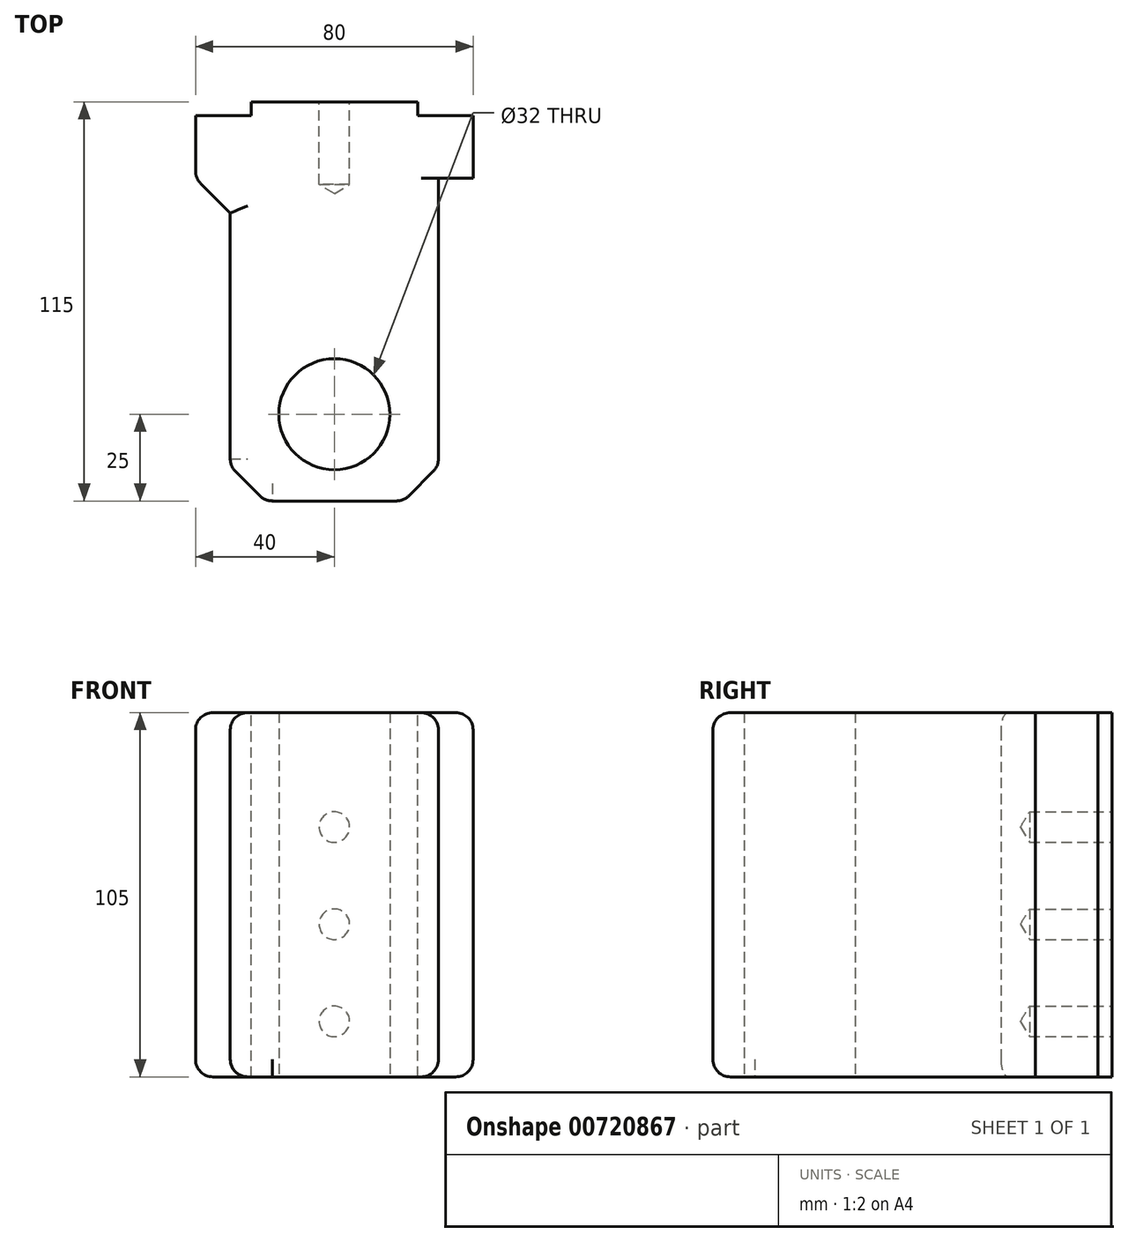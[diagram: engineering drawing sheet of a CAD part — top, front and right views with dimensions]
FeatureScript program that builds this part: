
annotation { "Feature Type Name" : "Feature", "Feature Type Description" : "" }
export const myFeature = defineFeature(function(context is Context, id is Id, definition is map)
    precondition{}
    {
        {
            var Q0;
            Q0=qCreatedBy(makeId("Front.planeOp"),FACE);
            var sketch = newSketch(context, id + "F0", { "sketchPlane" : qUnion([Q0])});
            skLineSegment(sketch, "E0.bottom", {"start": v(0, 0) * mm, "end": v(80, 0) * mm});
            skLineSegment(sketch, "E0.top", {"start": v(0, 105) * mm, "end": v(80, 105) * mm});
            skLineSegment(sketch, "E0.left", {"start": v(0, 0) * mm, "end": v(0, 105) * mm});
            skLineSegment(sketch, "E0.right", {"start": v(80, 0) * mm, "end": v(80, 105) * mm});
            skSolve(sketch);
        }
        {
            var Q0;
            Q0=makeQuery(id+"F0.imprint","IMPRINT",FACE,{"disambiguationData":[TD([[makeQuery(id+"F0.imprint","IMPRINT",EDGE,{"derivedFrom":sQuery(id+"F0.wireOp",EDGE,"E0.bottom")}),1.0]])]});
            extrude(context, id + "F1", {"entities" : qUnion([Q0]), "depth" : 22 * mm, "offsetDistance" : 25 * mm});
        }
        {
            var Q0;
            Q0=makeQuery(id+"F1.opExtrude","CAP_FACE",FACE,{"disambiguationData":[OSD([sQuery(id+"F0.wireOp",EDGE,"E0.bottom"),sQuery(id+"F0.wireOp",EDGE,"E0.top"),sQuery(id+"F0.wireOp",EDGE,"E0.left"),sQuery(id+"F0.wireOp",EDGE,"E0.right")])],"isStart":false});
            var sketch = newSketch(context, id + "F2", { "sketchPlane" : qUnion([Q0])});
            skPoint(sketch, "E1", {"position": v(10, 0) * mm});
            skLineSegment(sketch, "E2.bottom", {"start": v(10, 0) * mm, "end": v(70, 0) * mm});
            skLineSegment(sketch, "E2.top", {"start": v(10, 105) * mm, "end": v(70, 105) * mm});
            skLineSegment(sketch, "E2.left", {"start": v(10, 0) * mm, "end": v(10, 105) * mm});
            skLineSegment(sketch, "E2.right", {"start": v(70, 0) * mm, "end": v(70, 105) * mm});
            skSolve(sketch);
        }
        {
            var Q0;
            Q0=makeQuery(id+"F2.imprint","IMPRINT",FACE,{"disambiguationData":[TD([[makeQuery(id+"F2.imprint","IMPRINT",EDGE,{"derivedFrom":sQuery(id+"F2.wireOp",EDGE,"E2.bottom")}),1.0]])]});
            extrude(context, id + "F3", {"entities" : qUnion([Q0]), "operationType" : NewBodyOperationType.ADD, "depth" : 93 * mm, "offsetDistance" : 25 * mm});
        }
        {
            var Q0;
            Q0=makeQuery(id+"F3.opExtrude","CAP_EDGE",EDGE,{"disambiguationData":[OSD([sQuery(id+"F2.wireOp",EDGE,"E2.left")])],"isStart":true});
            var Q1;
            Q1=makeQuery(id+"F3.opExtrude","CAP_EDGE",EDGE,{"disambiguationData":[OSD([sQuery(id+"F2.wireOp",EDGE,"E2.right")])],"isStart":true});
            var Q2;
            Q2=makeQuery(id+"F3.opExtrude","CAP_EDGE",EDGE,{"disambiguationData":[OSD([sQuery(id+"F2.wireOp",EDGE,"E2.right")])],"isStart":false});
            var Q3;
            Q3=makeQuery(id+"F3.opExtrude","CAP_EDGE",EDGE,{"disambiguationData":[OSD([sQuery(id+"F2.wireOp",EDGE,"E2.left")])],"isStart":false});
            chamfer(context, id + "F4", {"entities" : qUnion([Q0, Q1, Q2, Q3]), "width" : 10 * mm, "tangentPropagation" : true});
        }
        {
            var Q0;
            Q0=makeQuery(id+"F1.opExtrude","CAP_FACE",FACE,{"disambiguationData":[OSD([sQuery(id+"F0.wireOp",EDGE,"E0.bottom"),sQuery(id+"F0.wireOp",EDGE,"E0.top"),sQuery(id+"F0.wireOp",EDGE,"E0.left"),sQuery(id+"F0.wireOp",EDGE,"E0.right")])],"isStart":true});
            var sketch = newSketch(context, id + "F5", { "sketchPlane" : qUnion([Q0])});
            skPoint(sketch, "E3", {"position": v(-64, 0) * mm});
            skPoint(sketch, "E4", {"position": v(-16, 0) * mm});
            skPoint(sketch, "E5", {"position": v(-40, 16) * mm});
            skPoint(sketch, "E5.positionSnap0", {"position": v(-40, 0) * mm});
            skPoint(sketch, "E6", {"position": v(-40, 44) * mm});
            skPoint(sketch, "E7", {"position": v(-40, 72) * mm});
            skLineSegment(sketch, "E8.bottom", {"start": v(-64, 0) * mm, "end": v(-80, 0) * mm});
            skLineSegment(sketch, "E8.top", {"start": v(-64, 105) * mm, "end": v(-80, 105) * mm});
            skLineSegment(sketch, "E8.left", {"start": v(-64, 0) * mm, "end": v(-64, 105) * mm});
            skLineSegment(sketch, "E8.right", {"start": v(-80, 0) * mm, "end": v(-80, 105) * mm});
            skLineSegment(sketch, "E9.bottom", {"start": v(-16, 0) * mm, "end": v(0, 0) * mm});
            skLineSegment(sketch, "E9.top", {"start": v(-16, 105) * mm, "end": v(0, 105) * mm});
            skLineSegment(sketch, "E9.left", {"start": v(-16, 0) * mm, "end": v(-16, 105) * mm});
            skLineSegment(sketch, "E9.right", {"start": v(0, 0) * mm, "end": v(0, 105) * mm});
            skSolve(sketch);
        }
        {
            var Q0;
            Q0=makeQuery(id+"F5.imprint","IMPRINT",FACE,{"disambiguationData":[TD([[makeQuery(id+"F5.imprint","IMPRINT",EDGE,{"derivedFrom":sQuery(id+"F5.wireOp",EDGE,"E8.bottom")}),-1.0]])]});
            var Q1;
            Q1=makeQuery(id+"F5.imprint","IMPRINT",FACE,{"disambiguationData":[TD([[makeQuery(id+"F5.imprint","IMPRINT",EDGE,{"derivedFrom":sQuery(id+"F5.wireOp",EDGE,"E9.bottom")}),-1.0]])]});
            extrude(context, id + "F6", {"entities" : qUnion([Q0, Q1]), "operationType" : NewBodyOperationType.REMOVE, "oppositeDirection" : true, "depth" : 3.96 * mm, "offsetDistance" : 25 * mm});
        }
        {
            var Q0;
            Q0=sQuery(id+"F5.wireOp",VERTEX,"E7");
            var Q1;
            Q1=sQuery(id+"F5.wireOp",VERTEX,"E6");
            var Q2;
            Q2=sQuery(id+"F5.wireOp",VERTEX,"E5");
            var Q3;
            Q3=makeQuery(id+"F1.opExtrude","SWEPT_BODY",BODY,{"disambiguationData":[OSD([sQuery(id+"F0.wireOp",EDGE,"E0.bottom"),sQuery(id+"F0.wireOp",EDGE,"E0.top"),sQuery(id+"F0.wireOp",EDGE,"E0.left"),sQuery(id+"F0.wireOp",EDGE,"E0.right")])]});
            hole(context, id + "F7", {"style" : HoleStyle.SIMPLE, "endStyle" : HoleEndStyle.BLIND, "standardTappedOrClearance" : lookupTablePath({ "standard" : "ISO", "engagement" : "75%", "pitch" : "1.25 mm", "size" : "M10", "type" : "Tapped" }), "standardBlindInLast" : lookupTablePath({ "standard" : "ISO", "engagement" : "75%", "pitch" : "1.25 mm", "size" : "M10", "type" : "Tapped" }), "holeDiameter" : 8.8 * mm, "majorDiameter" : 10 * mm, "showTappedDepth" : true, "holeDepth" : 23.75 * mm, "isTappedThrough" : true, "tappedDepth" : 20 * mm, "tapClearance" : 3, "locations" : qUnion([Q0, Q1, Q2]), "scope" : qUnion([Q3])});
        }
        {
            var Q0;
            Q0=makeQuery(id+"F3.boolean.opBoolean","MERGE",FACE,{"derivedFrom":[makeQuery(id+"F1.opExtrude","SWEPT_FACE",FACE,{"disambiguationData":[OSD([sQuery(id+"F0.wireOp",EDGE,"E0.bottom")])]}),makeQuery(id+"F3.opExtrude","SWEPT_FACE",FACE,{"disambiguationData":[OSD([sQuery(id+"F2.wireOp",EDGE,"E2.bottom")])]})]});
            var sketch = newSketch(context, id + "F8", { "sketchPlane" : qUnion([Q0])});
            skPoint(sketch, "E10", {"position": v(40, 90) * mm});
            skPoint(sketch, "E10.positionSnap0", {"position": v(40, 115) * mm});
            skCircle(sketch, "E11", {"center": v(40, 90) * mm, "radius": 16 * mm});
            skSolve(sketch);
        }
        {
            var Q0;
            Q0=makeQuery(id+"F8.imprint","IMPRINT",FACE,{"disambiguationData":[TD([[makeQuery(id+"F8.imprint","IMPRINT",EDGE,{"derivedFrom":sQuery(id+"F8.wireOp",EDGE,"E11")}),1.0]])]});
            extrude(context, id + "F9", {"entities" : qUnion([Q0]), "operationType" : NewBodyOperationType.REMOVE, "oppositeDirection" : true, "depth" : 120 * mm, "offsetDistance" : 25 * mm});
        }
        {
            var Q0;
            Q0=makeQuery(id+"F3.opExtrude","SWEPT_EDGE",EDGE,{"disambiguationData":[OSD([sQuery(id+"F0.wireOp",EDGE,"E0.top"),sQuery(id+"F2.wireOp",EDGE,"E2.top"),sQuery(id+"F2.wireOp",EDGE,"E2.right")])]});
            var Q1;
            Q1=makeQuery(id+"F4.opChamfer","BLEND_EDGE",EDGE,{"blendedFrom":[makeQuery(id+"F3.opExtrude","CAP_EDGE",EDGE,{"disambiguationData":[OSD([sQuery(id+"F2.wireOp",EDGE,"E2.right")])],"isStart":false}),makeQuery(id+"F3.boolean.opBoolean","MERGE",FACE,{"derivedFrom":[makeQuery(id+"F1.opExtrude","SWEPT_FACE",FACE,{"disambiguationData":[OSD([sQuery(id+"F0.wireOp",EDGE,"E0.top")])]}),makeQuery(id+"F3.opExtrude","SWEPT_FACE",FACE,{"disambiguationData":[OSD([sQuery(id+"F2.wireOp",EDGE,"E2.top")])]})]})],"blendedInto":[makeQuery(id+"F3.boolean.opBoolean","MERGE",FACE,{"derivedFrom":[makeQuery(id+"F1.opExtrude","SWEPT_FACE",FACE,{"disambiguationData":[OSD([sQuery(id+"F0.wireOp",EDGE,"E0.top")])]}),makeQuery(id+"F3.opExtrude","SWEPT_FACE",FACE,{"disambiguationData":[OSD([sQuery(id+"F2.wireOp",EDGE,"E2.top")])]})]})]});
            var Q2;
            Q2=makeQuery(id+"F3.opExtrude","CAP_EDGE",EDGE,{"disambiguationData":[OSD([sQuery(id+"F2.wireOp",EDGE,"E2.top")])],"isStart":false});
            var Q3;
            Q3=makeQuery(id+"F4.opChamfer","BLEND_EDGE",EDGE,{"blendedFrom":[makeQuery(id+"F3.opExtrude","CAP_EDGE",EDGE,{"disambiguationData":[OSD([sQuery(id+"F2.wireOp",EDGE,"E2.left")])],"isStart":false}),makeQuery(id+"F3.boolean.opBoolean","MERGE",FACE,{"derivedFrom":[makeQuery(id+"F1.opExtrude","SWEPT_FACE",FACE,{"disambiguationData":[OSD([sQuery(id+"F0.wireOp",EDGE,"E0.top")])]}),makeQuery(id+"F3.opExtrude","SWEPT_FACE",FACE,{"disambiguationData":[OSD([sQuery(id+"F2.wireOp",EDGE,"E2.top")])]})]})],"blendedInto":[makeQuery(id+"F3.boolean.opBoolean","MERGE",FACE,{"derivedFrom":[makeQuery(id+"F1.opExtrude","SWEPT_FACE",FACE,{"disambiguationData":[OSD([sQuery(id+"F0.wireOp",EDGE,"E0.top")])]}),makeQuery(id+"F3.opExtrude","SWEPT_FACE",FACE,{"disambiguationData":[OSD([sQuery(id+"F2.wireOp",EDGE,"E2.top")])]})]})]});
            var Q4;
            Q4=makeQuery(id+"F3.opExtrude","SWEPT_EDGE",EDGE,{"disambiguationData":[OSD([sQuery(id+"F0.wireOp",EDGE,"E0.top"),sQuery(id+"F2.wireOp",EDGE,"E2.top"),sQuery(id+"F2.wireOp",EDGE,"E2.left")])]});
            var Q5;
            Q5=makeQuery(id+"F4.opChamfer","BLEND_EDGE",EDGE,{"blendedFrom":[makeQuery(id+"F3.opExtrude","CAP_EDGE",EDGE,{"disambiguationData":[OSD([sQuery(id+"F2.wireOp",EDGE,"E2.left")])],"isStart":true}),makeQuery(id+"F3.boolean.opBoolean","MERGE",FACE,{"derivedFrom":[makeQuery(id+"F1.opExtrude","SWEPT_FACE",FACE,{"disambiguationData":[OSD([sQuery(id+"F0.wireOp",EDGE,"E0.top")])]}),makeQuery(id+"F3.opExtrude","SWEPT_FACE",FACE,{"disambiguationData":[OSD([sQuery(id+"F2.wireOp",EDGE,"E2.top")])]})]})],"blendedInto":[makeQuery(id+"F3.boolean.opBoolean","MERGE",FACE,{"derivedFrom":[makeQuery(id+"F1.opExtrude","SWEPT_FACE",FACE,{"disambiguationData":[OSD([sQuery(id+"F0.wireOp",EDGE,"E0.top")])]}),makeQuery(id+"F3.opExtrude","SWEPT_FACE",FACE,{"disambiguationData":[OSD([sQuery(id+"F2.wireOp",EDGE,"E2.top")])]})]})]});
            var Q6;
            Q6=makeQuery(id+"F1.opExtrude","SWEPT_EDGE",EDGE,{"disambiguationData":[OSD([sQuery(id+"F0.wireOp",EDGE,"E0.top"),sQuery(id+"F0.wireOp",EDGE,"E0.left")])]});
            var Q7;
            Q7=makeQuery(id+"F1.opExtrude","SWEPT_EDGE",EDGE,{"disambiguationData":[OSD([sQuery(id+"F0.wireOp",EDGE,"E0.top"),sQuery(id+"F0.wireOp",EDGE,"E0.right")])]});
            var Q8;
            Q8=makeQuery(id+"F4.opChamfer","BLEND_EDGE",EDGE,{"blendedFrom":[makeQuery(id+"F3.opExtrude","CAP_EDGE",EDGE,{"disambiguationData":[OSD([sQuery(id+"F2.wireOp",EDGE,"E2.right")])],"isStart":true}),makeQuery(id+"F3.boolean.opBoolean","MERGE",FACE,{"derivedFrom":[makeQuery(id+"F1.opExtrude","SWEPT_FACE",FACE,{"disambiguationData":[OSD([sQuery(id+"F0.wireOp",EDGE,"E0.top")])]}),makeQuery(id+"F3.opExtrude","SWEPT_FACE",FACE,{"disambiguationData":[OSD([sQuery(id+"F2.wireOp",EDGE,"E2.top")])]})]})],"blendedInto":[makeQuery(id+"F3.boolean.opBoolean","MERGE",FACE,{"derivedFrom":[makeQuery(id+"F1.opExtrude","SWEPT_FACE",FACE,{"disambiguationData":[OSD([sQuery(id+"F0.wireOp",EDGE,"E0.top")])]}),makeQuery(id+"F3.opExtrude","SWEPT_FACE",FACE,{"disambiguationData":[OSD([sQuery(id+"F2.wireOp",EDGE,"E2.top")])]})]})]});
            var Q9;
            Q9=makeQuery(id+"F4.opChamfer","BLEND_EDGE",EDGE,{"blendedFrom":[makeQuery(id+"F3.opExtrude","CAP_EDGE",EDGE,{"disambiguationData":[OSD([sQuery(id+"F2.wireOp",EDGE,"E2.right")])],"isStart":true}),makeQuery(id+"F1.opExtrude","SWEPT_FACE",FACE,{"disambiguationData":[OSD([sQuery(id+"F0.wireOp",EDGE,"E0.right")])]})],"blendedInto":[makeQuery(id+"F1.opExtrude","SWEPT_FACE",FACE,{"disambiguationData":[OSD([sQuery(id+"F0.wireOp",EDGE,"E0.right")])]})]});
            var Q10;
            Q10=makeQuery(id+"F4.opChamfer","BLEND_EDGE",EDGE,{"blendedFrom":[makeQuery(id+"F3.opExtrude","CAP_EDGE",EDGE,{"disambiguationData":[OSD([sQuery(id+"F2.wireOp",EDGE,"E2.left")])],"isStart":true}),makeQuery(id+"F1.opExtrude","SWEPT_FACE",FACE,{"disambiguationData":[OSD([sQuery(id+"F0.wireOp",EDGE,"E0.left")])]})],"blendedInto":[makeQuery(id+"F1.opExtrude","SWEPT_FACE",FACE,{"disambiguationData":[OSD([sQuery(id+"F0.wireOp",EDGE,"E0.left")])]})]});
            var Q11;
            Q11=makeQuery(id+"F3.opExtrude","SWEPT_EDGE",EDGE,{"disambiguationData":[OSD([sQuery(id+"F0.wireOp",EDGE,"E0.bottom"),sQuery(id+"F2.wireOp",EDGE,"E2.bottom"),sQuery(id+"F2.wireOp",EDGE,"E2.left")])]});
            var Q12;
            Q12=makeQuery(id+"F4.opChamfer","BLEND_EDGE",EDGE,{"blendedFrom":[makeQuery(id+"F3.opExtrude","CAP_EDGE",EDGE,{"disambiguationData":[OSD([sQuery(id+"F2.wireOp",EDGE,"E2.left")])],"isStart":true}),makeQuery(id+"F3.boolean.opBoolean","MERGE",FACE,{"derivedFrom":[makeQuery(id+"F1.opExtrude","SWEPT_FACE",FACE,{"disambiguationData":[OSD([sQuery(id+"F0.wireOp",EDGE,"E0.bottom")])]}),makeQuery(id+"F3.opExtrude","SWEPT_FACE",FACE,{"disambiguationData":[OSD([sQuery(id+"F2.wireOp",EDGE,"E2.bottom")])]})]})],"blendedInto":[makeQuery(id+"F3.boolean.opBoolean","MERGE",FACE,{"derivedFrom":[makeQuery(id+"F1.opExtrude","SWEPT_FACE",FACE,{"disambiguationData":[OSD([sQuery(id+"F0.wireOp",EDGE,"E0.bottom")])]}),makeQuery(id+"F3.opExtrude","SWEPT_FACE",FACE,{"disambiguationData":[OSD([sQuery(id+"F2.wireOp",EDGE,"E2.bottom")])]})]})]});
            var Q13;
            Q13=makeQuery(id+"F1.opExtrude","SWEPT_EDGE",EDGE,{"disambiguationData":[OSD([sQuery(id+"F0.wireOp",EDGE,"E0.bottom"),sQuery(id+"F0.wireOp",EDGE,"E0.left")])]});
            var Q14;
            Q14=makeQuery(id+"F3.opExtrude","SWEPT_EDGE",EDGE,{"disambiguationData":[OSD([sQuery(id+"F0.wireOp",EDGE,"E0.bottom"),sQuery(id+"F2.wireOp",EDGE,"E2.bottom"),sQuery(id+"F2.wireOp",EDGE,"E2.right")])]});
            var Q15;
            Q15=makeQuery(id+"F4.opChamfer","BLEND_EDGE",EDGE,{"blendedFrom":[makeQuery(id+"F3.opExtrude","CAP_EDGE",EDGE,{"disambiguationData":[OSD([sQuery(id+"F2.wireOp",EDGE,"E2.right")])],"isStart":false}),makeQuery(id+"F3.boolean.opBoolean","MERGE",FACE,{"derivedFrom":[makeQuery(id+"F1.opExtrude","SWEPT_FACE",FACE,{"disambiguationData":[OSD([sQuery(id+"F0.wireOp",EDGE,"E0.bottom")])]}),makeQuery(id+"F3.opExtrude","SWEPT_FACE",FACE,{"disambiguationData":[OSD([sQuery(id+"F2.wireOp",EDGE,"E2.bottom")])]})]})],"blendedInto":[makeQuery(id+"F3.boolean.opBoolean","MERGE",FACE,{"derivedFrom":[makeQuery(id+"F1.opExtrude","SWEPT_FACE",FACE,{"disambiguationData":[OSD([sQuery(id+"F0.wireOp",EDGE,"E0.bottom")])]}),makeQuery(id+"F3.opExtrude","SWEPT_FACE",FACE,{"disambiguationData":[OSD([sQuery(id+"F2.wireOp",EDGE,"E2.bottom")])]})]})]});
            var Q16;
            Q16=makeQuery(id+"F3.opExtrude","CAP_EDGE",EDGE,{"disambiguationData":[OSD([sQuery(id+"F2.wireOp",EDGE,"E2.bottom")])],"isStart":false});
            var Q17;
            Q17=makeQuery(id+"F4.opChamfer","BLEND_EDGE",EDGE,{"blendedFrom":[makeQuery(id+"F3.opExtrude","CAP_EDGE",EDGE,{"disambiguationData":[OSD([sQuery(id+"F2.wireOp",EDGE,"E2.right")])],"isStart":true}),makeQuery(id+"F3.boolean.opBoolean","MERGE",FACE,{"derivedFrom":[makeQuery(id+"F1.opExtrude","SWEPT_FACE",FACE,{"disambiguationData":[OSD([sQuery(id+"F0.wireOp",EDGE,"E0.bottom")])]}),makeQuery(id+"F3.opExtrude","SWEPT_FACE",FACE,{"disambiguationData":[OSD([sQuery(id+"F2.wireOp",EDGE,"E2.bottom")])]})]})],"blendedInto":[makeQuery(id+"F3.boolean.opBoolean","MERGE",FACE,{"derivedFrom":[makeQuery(id+"F1.opExtrude","SWEPT_FACE",FACE,{"disambiguationData":[OSD([sQuery(id+"F0.wireOp",EDGE,"E0.bottom")])]}),makeQuery(id+"F3.opExtrude","SWEPT_FACE",FACE,{"disambiguationData":[OSD([sQuery(id+"F2.wireOp",EDGE,"E2.bottom")])]})]})]});
            var Q18;
            Q18=makeQuery(id+"F1.opExtrude","SWEPT_EDGE",EDGE,{"disambiguationData":[OSD([sQuery(id+"F0.wireOp",EDGE,"E0.bottom"),sQuery(id+"F0.wireOp",EDGE,"E0.right")])]});
            fillet(context, id + "F10", {"entities" : qUnion([Q0, Q1, Q2, Q3, Q4, Q5, Q6, Q7, Q8, Q9, Q10, Q11, Q12, Q13, Q14, Q15, Q16, Q17, Q18]), "radius" : 5 * mm, "tangentPropagation" : true, "allowEdgeOverflow" : false});
        }
        {
            var Q0;
            {var subQ0=sQuery(id+"F2.wireOp",EDGE,"E2.left");Q0=makeQuery(id+"F10.opFillet","BLEND_EDGE",EDGE,{"blendedFrom":[makeQuery(id+"F3.opExtrude","CAP_EDGE",EDGE,{"disambiguationData":[OSD([sQuery(id+"F2.wireOp",EDGE,"E2.bottom")])],"isStart":false}),makeQuery(id+"F4.opChamfer","BLEND_FACE",FACE,{"disambiguationData":[OSD([subQ0]),TDD([makeQuery(id+"F3.opExtrude","CAP_EDGE",EDGE,{"disambiguationData":[OSD([subQ0])],"isStart":false})])]})],"blendedInto":[makeQuery(id+"F4.opChamfer","BLEND_FACE",FACE,{"disambiguationData":[OSD([subQ0]),TDD([makeQuery(id+"F3.opExtrude","CAP_EDGE",EDGE,{"disambiguationData":[OSD([subQ0])],"isStart":false})])]})]});}
            var Q1;
            {var subQ0=sQuery(id+"F2.wireOp",EDGE,"E2.right");Q1=makeQuery(id+"F4.opChamfer","BLEND_FACE",FACE,{"disambiguationData":[OSD([subQ0]),TDD([makeQuery(id+"F3.opExtrude","CAP_EDGE",EDGE,{"disambiguationData":[OSD([subQ0])],"isStart":false})])]});}
            fillet(context, id + "F11", {"entities" : qUnion([Q0, Q1]), "radius" : 5 * mm, "tangentPropagation" : true, "allowEdgeOverflow" : false});
        }
    });
